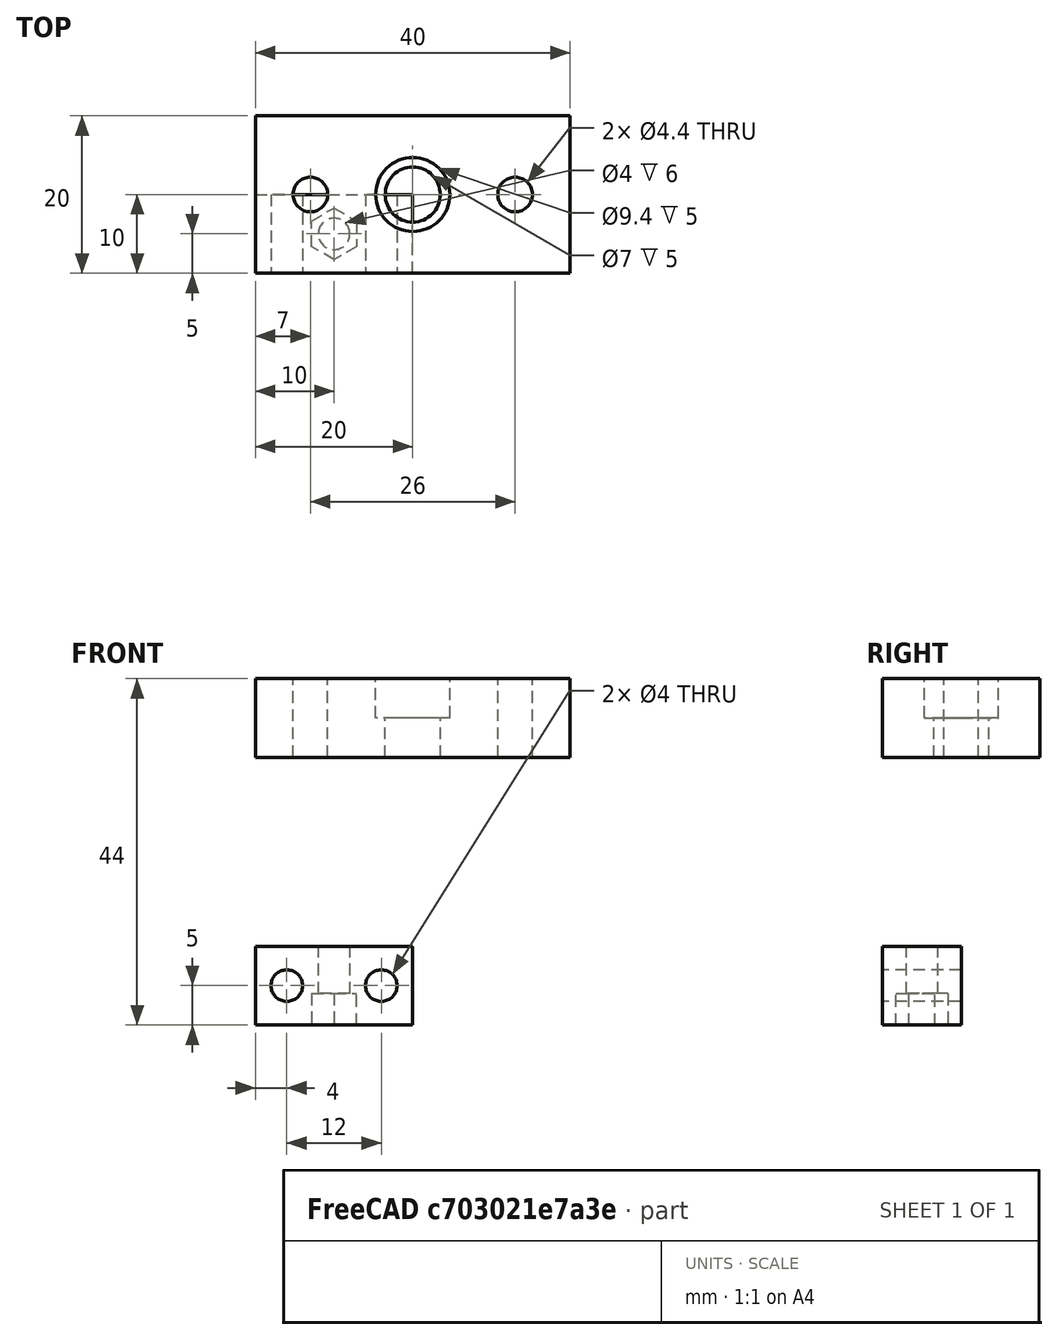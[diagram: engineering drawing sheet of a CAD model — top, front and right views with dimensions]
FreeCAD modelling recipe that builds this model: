
FCSTD DOCUMENT  (FreeCAD 0.16R6703 (Git))
Label: force-test
License: All rights reserved
LicenseURL: http://en.wikipedia.org/wiki/All_rights_reserved
objects: Part::Cylinder×8, Part::Feature×5, Part::MultiFuse×5, Part::Cut×5, Part::Box×3
note: 26 computed .brp shape members not serialized (recipe doc carries the construction recipe); baked Part::Feature solids carry a one-line shape summary decoded from their .brp

FEATURE [Part::Box] Box  label="Cube"
  Height = 10
  Length = 20
  Width = 10
FEATURE [Part::Cylinder] Cylinder
  Angle = 360
  Height = 15
  Placement = pos=(10,5,-2) rot=(0,0,1;0rad)
  Radius = 2
FEATURE [Part::Cylinder] Cylinder001
  Angle = 360
  Height = 8
  Placement = pos=(0,0,1) rot=(0,0,1;0rad)
  Radius = 4
FEATURE [Part::Box] Box001  label="Cube001"
  Height = 10
  Length = 10
  Placement = pos=(-12.85,-5,0) rot=(0,0,1;0rad)
  Width = 10
FEATURE [Part::Feature] Box001001
  Placement = pos=(-2.09487,-13.6284,0) rot=(0,0,1;1.0472rad)
  shape: bbox 13.66 x 13.66 x 10 mm, 6 faces (baked)
FEATURE [Part::Feature] Box001002
  Placement = pos=(10.7551,-8.62843,0) rot=(0,0,1;2.0944rad)
  shape: bbox 13.66 x 13.66 x 10 mm, 6 faces (baked)
FEATURE [Part::Feature] Box001003
  Placement = pos=(12.85,5,0) rot=(0,0,1;3.14159rad)
  shape: bbox 10 x 10 x 10 mm, 6 faces (baked)
FEATURE [Part::Feature] Box001004
  Placement = pos=(2.09487,13.6284,0) rot=(0,0,1;4.18879rad)
  shape: bbox 13.66 x 13.66 x 10 mm, 6 faces (baked)
FEATURE [Part::Feature] Box001005
  Placement = pos=(-10.7551,8.62843,0) rot=(0,0,-1;1.0472rad)
  shape: bbox 13.66 x 13.66 x 10 mm, 6 faces (baked)
FEATURE [Part::MultiFuse] Fusion
  Shapes = -> [Box001,Box001005,Box001001,Box001002,Box001003,Box001004]
FEATURE [Part::Cut] Cut
  Base = -> Cylinder001
  Placement = pos=(10,5,-5) rot=(0,0,1;0rad)
  Tool = -> Fusion
FEATURE [Part::MultiFuse] Fusion001
  Shapes = -> [Cylinder,Cut]
FEATURE [Part::Cut] Cut001
  Base = -> Box
  Tool = -> Fusion001
FEATURE [Part::Cylinder] Cylinder002
  Angle = 360
  Height = 18
  Placement = pos=(4,11,5) rot=(1,0,0;1.5708rad)
  Radius = 2
FEATURE [Part::Cylinder] Cylinder003
  Angle = 360
  Height = 18
  Placement = pos=(16,11,5) rot=(1,0,0;1.5708rad)
  Radius = 2
FEATURE [Part::MultiFuse] Fusion002
  Shapes = -> [Cylinder002,Cylinder003]
FEATURE [Part::Cut] Cut002
  Base = -> Cut001
  Tool = -> Fusion002
FEATURE [Part::Box] Box001006  label="Cube002"
  Height = 10
  Length = 40
  Width = 20
FEATURE [Part::Cylinder] Cylinder004
  Angle = 360
  Height = 15
  Placement = pos=(20,10,-1) rot=(0,0,1;0rad)
  Radius = 3.5
FEATURE [Part::Cylinder] Cylinder005
  Angle = 360
  Height = 15
  Placement = pos=(20,10,5) rot=(0,0,1;0rad)
  Radius = 4.7
FEATURE [Part::Cylinder] Cylinder006
  Angle = 360
  Height = 15
  Placement = pos=(7,10,-1) rot=(0,0,1;0rad)
  Radius = 2.2
FEATURE [Part::MultiFuse] Fusion003
  Shapes = -> [Cylinder004,Cylinder005]
FEATURE [Part::Cut] Cut003
  Base = -> Box001006
  Tool = -> Fusion003
FEATURE [Part::Cylinder] Cylinder007
  Angle = 360
  Height = 15
  Placement = pos=(33,10,-1) rot=(0,0,1;0rad)
  Radius = 2.2
FEATURE [Part::MultiFuse] Fusion004
  Shapes = -> [Cylinder006,Cylinder007]
FEATURE [Part::Cut] Cut004
  Base = -> Cut003
  Placement = pos=(0,0,34) rot=(0,0,1;0rad)
  Tool = -> Fusion004
